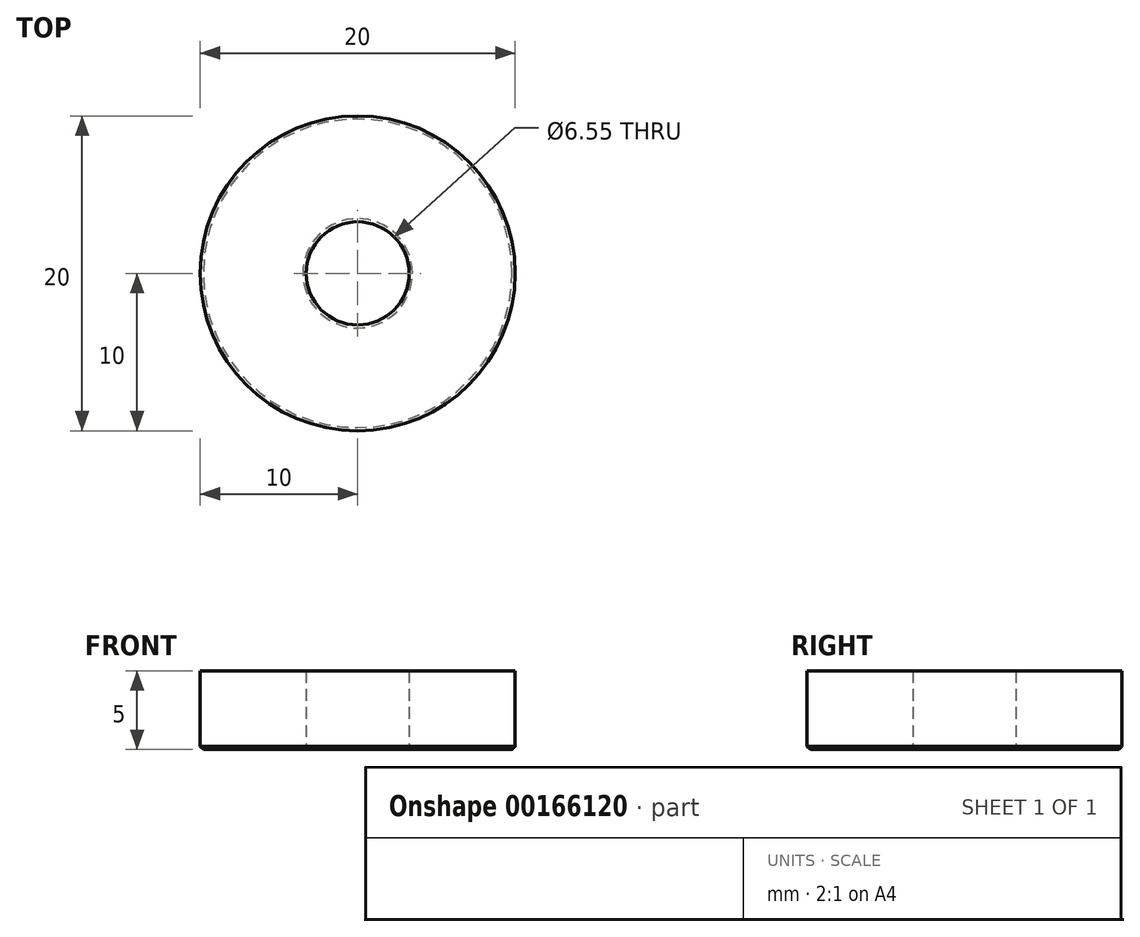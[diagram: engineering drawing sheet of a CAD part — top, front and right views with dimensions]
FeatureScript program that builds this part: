
annotation { "Feature Type Name" : "Feature", "Feature Type Description" : "" }
export const myFeature = defineFeature(function(context is Context, id is Id, definition is map)
    precondition{}
    {
        {
            var Q0;
            Q0=qCreatedBy(makeId("Top.planeOp"),FACE);
            var sketch = newSketch(context, id + "F0", { "sketchPlane" : qUnion([Q0])});
            skCircle(sketch, "E0", {"center": v(0, 0) * mm, "radius": 3.28 * mm});
            skCircle(sketch, "E1", {"center": v(0, 0) * mm, "radius": 10 * mm});
            skSolve(sketch);
        }
        {
            var Q0;
            Q0 = qSketchRegion(id + "F0", true);
            extrude(context, id + "F1", {"entities" : qUnion([Q0]), "depth" : 5 * mm});
        }
        {
            var Q0;
            Q0=makeQuery(id+"F1.opExtrude","CAP_FACE",FACE,{"disambiguationData":[OSD([sQuery(id+"F0.wireOp",EDGE,"E0"),sQuery(id+"F0.wireOp",EDGE,"E1")])],"isStart":true});
            chamfer(context, id + "F2", {"entities" : qUnion([Q0]), "width" : 0.2 * mm});
        }
    });
